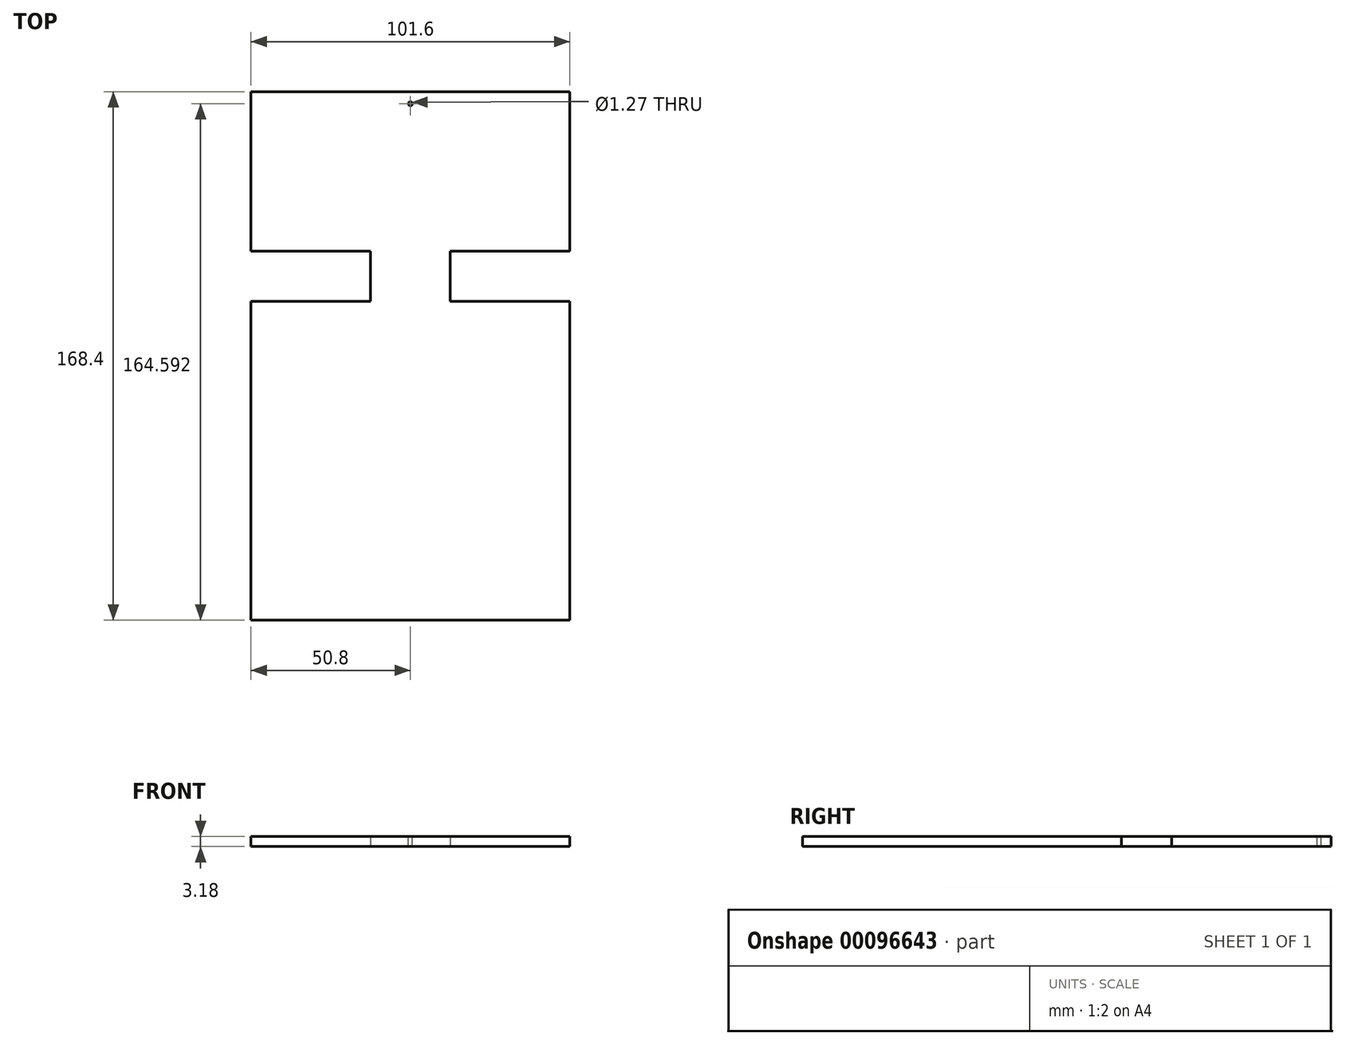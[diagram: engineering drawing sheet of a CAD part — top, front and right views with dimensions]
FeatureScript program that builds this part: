
annotation { "Feature Type Name" : "Feature", "Feature Type Description" : "" }
export const myFeature = defineFeature(function(context is Context, id is Id, definition is map)
    precondition{}
    {
        {
            var Q0;
            Q0=qCreatedBy(makeId("Top.planeOp"),FACE);
            var sketch = newSketch(context, id + "F0", { "sketchPlane" : qUnion([Q0])});
            skLineSegment(sketch, "E0", {"start": v(0, 0) * mm, "end": v(-50.8, 0) * mm});
            skLineSegment(sketch, "E1", {"start": v(-50.8, 0) * mm, "end": v(-50.8, 101.6) * mm});
            skLineSegment(sketch, "E2", {"start": v(-50.8, 101.6) * mm, "end": v(-12.7, 101.6) * mm});
            skLineSegment(sketch, "E3", {"start": v(-12.7, 101.6) * mm, "end": v(-12.7, 117.6) * mm});
            skLineSegment(sketch, "E4", {"start": v(-12.7, 117.6) * mm, "end": v(-50.8, 117.6) * mm});
            skLineSegment(sketch, "E5", {"start": v(-50.8, 117.6) * mm, "end": v(-50.8, 168.4) * mm});
            skLineSegment(sketch, "E6", {"start": v(-50.8, 168.4) * mm, "end": v(0, 168.4) * mm});
            skLineSegment(sketch, "E7", {"start": v(0, 168.4) * mm, "end": v(0, 0) * mm});
            skLineSegment(sketch, "E8.MirrorCS", {"start": v(50.8, 0) * mm, "end": v(50.8, 101.6) * mm});
            skLineSegment(sketch, "E9.MirrorCS", {"start": v(0, 0) * mm, "end": v(50.8, 0) * mm});
            skLineSegment(sketch, "E10.MirrorCS", {"start": v(50.8, 168.4) * mm, "end": v(0, 168.4) * mm});
            skLineSegment(sketch, "E11.MirrorCS", {"start": v(50.8, 101.6) * mm, "end": v(12.7, 101.6) * mm});
            skLineSegment(sketch, "E12.MirrorCS", {"start": v(12.7, 117.6) * mm, "end": v(50.8, 117.6) * mm});
            skLineSegment(sketch, "E13.MirrorCS", {"start": v(12.7, 101.6) * mm, "end": v(12.7, 117.6) * mm});
            skLineSegment(sketch, "E14.MirrorCS", {"start": v(50.8, 117.6) * mm, "end": v(50.8, 168.4) * mm});
            skSolve(sketch);
        }
        {
            var Q0;
            Q0 = qSketchRegion(id + "F0", true);
            extrude(context, id + "F1", {"entities" : qUnion([Q0]), "depth" : 3.17 * mm});
        }
        {
            var Q0;
            Q0=makeQuery(id+"F1.opExtrude","CAP_FACE",FACE,{"disambiguationData":[OSD([sQuery(id+"F0.wireOp",EDGE,"E0"),sQuery(id+"F0.wireOp",EDGE,"E1"),sQuery(id+"F0.wireOp",EDGE,"E2"),sQuery(id+"F0.wireOp",EDGE,"E3"),sQuery(id+"F0.wireOp",EDGE,"E4"),sQuery(id+"F0.wireOp",EDGE,"E5"),sQuery(id+"F0.wireOp",EDGE,"E6"),sQuery(id+"F0.wireOp",EDGE,"E8.MirrorCS"),sQuery(id+"F0.wireOp",EDGE,"E9.MirrorCS"),sQuery(id+"F0.wireOp",EDGE,"E10.MirrorCS"),sQuery(id+"F0.wireOp",EDGE,"E11.MirrorCS"),sQuery(id+"F0.wireOp",EDGE,"E12.MirrorCS"),sQuery(id+"F0.wireOp",EDGE,"E13.MirrorCS"),sQuery(id+"F0.wireOp",EDGE,"E14.MirrorCS")])],"isStart":false});
            var sketch = newSketch(context, id + "F2", { "sketchPlane" : qUnion([Q0])});
            skCircle(sketch, "E15", {"center": v(0, 164.6) * mm, "radius": 0.64 * mm});
            skSolve(sketch);
        }
        {
            var Q0;
            Q0 = qSketchRegion(id + "F2", true);
            extrude(context, id + "F3", {"entities" : qUnion([Q0]), "operationType" : NewBodyOperationType.REMOVE, "endBound" : BoundingType.THROUGH_ALL, "oppositeDirection" : true, "depth" : 25.4 * mm});
        }
    });
